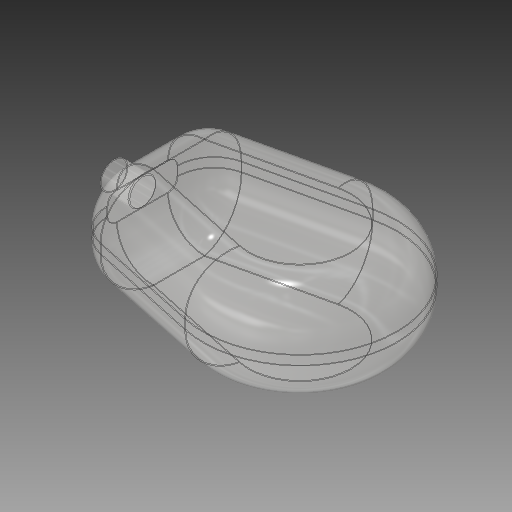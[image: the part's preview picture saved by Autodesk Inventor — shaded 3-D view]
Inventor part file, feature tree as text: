
AUTODESK INVENTOR PART (.ipt)
format: ipt  version: 2019 (Build 230136000, 136)  size: 340,480 bytes
history: native  units: mm
features: other x4, extrude x2, fillet x2, sketch x2, shell x1
ambient origin geometry x8: Origin, YZ Plane, XZ Plane, XY Plane, X Axis, Y Axis, Z Axis, Center Point
bodies: Body1 (feature_tree)
feature tree (11):
  other  "Sólido1"
  extrude  "Extrusão1"  Depth=70.0mm
  fillet  "Arredondamento1"  Radius=8.0mm
  fillet  "Arredondamento2"  Radius=170.0mm
  extrude  "Extrusão2"  Depth=40.0mm TaperAngle=0.0deg
  shell  "Casca1"  Thickness=50.0mm
  sketch  "Esboço1"  dims[d0=70.0mm d1=70.0mm d2=8.0mm d3=170.0mm]
  other  "Referência1"
  sketch  "Esboço2"  dims[d4=210.0mm d5=110.0mm d6=0.0mm d7=50.0mm d8=40.0mm d9=30.0mm d10=30.0mm d11=0.0mm d13=1.0mm]
  other  "Conjunto Ambu.iam"
  other  "Tampa de Entrada:1"
